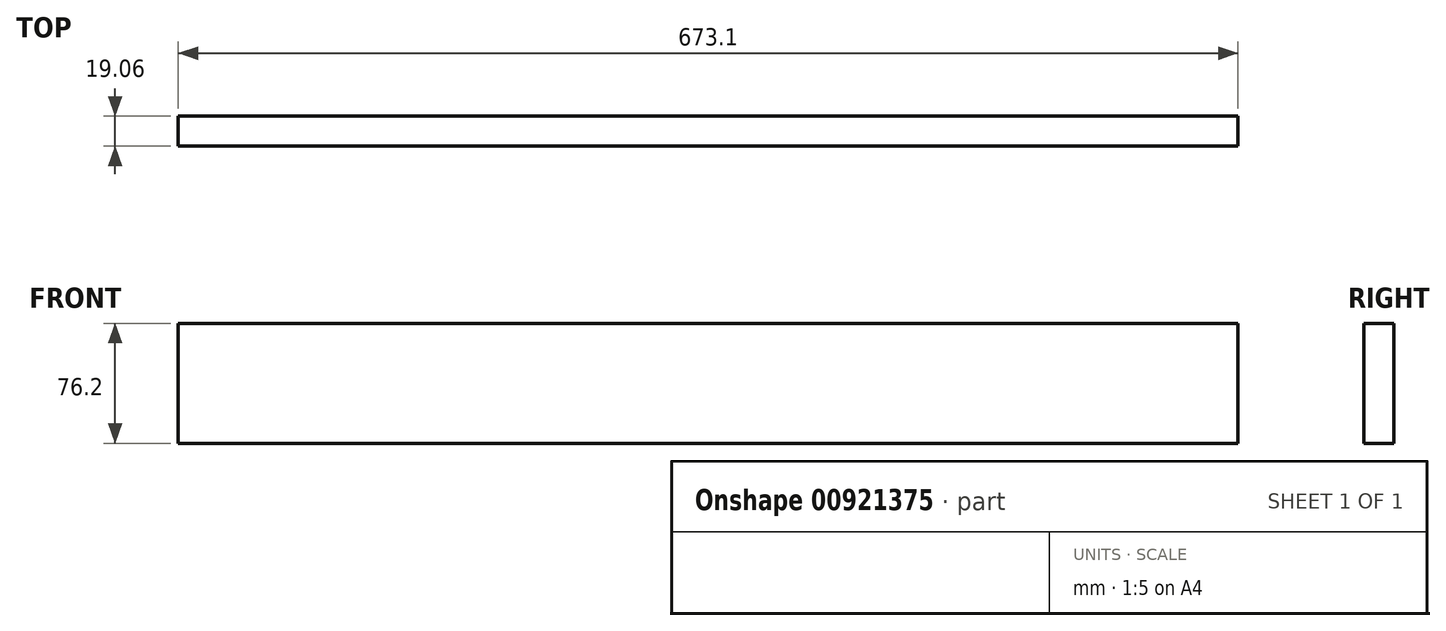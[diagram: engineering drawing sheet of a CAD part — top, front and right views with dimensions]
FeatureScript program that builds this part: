
annotation { "Feature Type Name" : "Feature", "Feature Type Description" : "" }
export const myFeature = defineFeature(function(context is Context, id is Id, definition is map)
    precondition{}
    {
        {
            var Q0;
            Q0=qCreatedBy(makeId("Right.planeOp"),FACE);
            var sketch = newSketch(context, id + "F0", { "sketchPlane" : qUnion([Q0])});
            skLineSegment(sketch, "E0.bottom", {"start": v(-9.53, 38.1) * mm, "end": v(9.53, 38.1) * mm});
            skLineSegment(sketch, "E0.top", {"start": v(-9.53, -38.1) * mm, "end": v(9.52, -38.1) * mm});
            skLineSegment(sketch, "E0.left", {"start": v(-9.53, 38.1) * mm, "end": v(-9.53, -38.1) * mm});
            skLineSegment(sketch, "E0.right", {"start": v(9.53, 38.1) * mm, "end": v(9.52, -38.1) * mm});
            skLineSegment(sketch, "E1", {"start": v(-9.52, 38.1) * mm, "end": v(9.52, -38.1) * mm, "construction": true});
            skSolve(sketch);
        }
        {
            var Q0;
            Q0 = qSketchRegion(id + "F0", true);
            extrude(context, id + "F1", {"entities" : qUnion([Q0]), "endBound" : BoundingType.SYMMETRIC, "depth" : 673.1 * mm, "offsetDistance" : 25.4 * mm});
        }
    });
